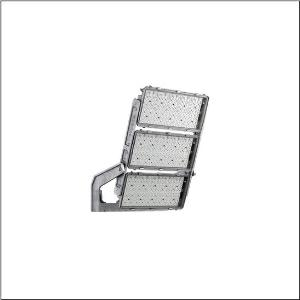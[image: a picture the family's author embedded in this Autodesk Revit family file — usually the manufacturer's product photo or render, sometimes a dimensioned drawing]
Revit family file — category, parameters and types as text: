
# Revit family: floodlight_fl_11_maxi_pro_remote___pl64blc_5xa779425w01aa_643d
name_source: partatom
category: Lighting Fixtures
units: mm (PartAtom-declared; Revit-internal decimal feet)

## family parameters
Cut with Voids When Loaded = No
Host = Face
Light Source = No
Part Type = Normal
Room Calculation Point = No
Round Connector Dimension = Use Diameter
Shared = No

## types (1)
- --- (1 x LED, 135060 lm, 1516.7 W, 3000K)
    Apparent Load = 1517 VA
    CIE Flux Codes = 28 83 99 100 100
    Color Rendering = 70
    Color Temperature = 3000K
    Default Elevation = 1800 mm
    Description = Floodlight FL 11  maxi  pro Remote floodlight; light control with lens of PMMA; cover panel of toughened safety glass, transparent; light distribution: PL64BLC, asymmetric direct distribution, LEDcolour temperature: 3000K, rated luminous flux: 135.060lm, colour rendering: CRI > 70, light colour: 730; luminous efficacy: 89lm/W; brightness control: DALI 2 (1 DALI address); with terminal, 8-pole, max. 2.5mm², mains connection: 220..240V/380..400V AC, 50/60Hz, surge voltage resistance: line to ground: 10kV, ECG replaceable separately, no afterglow with DALI off / DMX off command, LED unit replaceable without ESD environment, dustproof LED module, dimming range 10..100%; 1517W floodlight with 2x LED unit of diecast aluminium, coated grey; length: 713mm / width: 651mm / height: 338mm; mounting bracket, of diecast aluminium, uncoated, natural, equipment: Power, protection rating (complete): IP66; insulation class (complete): insulation class I (protective earthing); certification: CE, ENEC, VDE; ball protection: ball impact resistance with accessories, impact resistance: IK07; only for outdoor installations, rated ambient temperature 10°C, permissible operating ambient temperature: -40..+30°C, permissible storage temperature: -40..+85°C; packaging unit: 1 piece

Light Distribution: PL64BLC
    Height = 320 mm
    Lamp = 1 x LED
    Lamp Light Flux = 135060 lm
    Lamp Power = 1516.7 W
    Lamp count = 1
    Length = 1002 mm
    Luminous efficacy = 89 lm/W
    Manufacturer = Siteco
    ModVariant = No
    Model = 5XA779425W01AA
    Mounting Place = Ceiling
    Mounting Type = Surface mounted
    Number of Poles = 1
    OnlyDefault = Yes
    Power Factor = 1
    Product Name = Floodlight FL 11 maxi pro Remote | PL64BLC
    Product group = floodlight | ceiling mounted
    ProductGroupID = 302
    Protection Class = Protection class I
    Protection Degree = IP 66
    RLX_Detail_Level = 1
    RLX_Emergency_Light_Flux = 0 lm
    RLX_Emergency_Type = 0
    RLX_Emergency_Type_DB = No
    RlxData = <blob elided: 52317 chars, md5=75fceba1>
    Socket = socket
    Standby Power = 0 W
    System Light Flux = 135060 lm
    System Power = 1517 W
    Type Comments = factory setting: luminous flux: 100 % | dim-lin: 254 | 1070 mA
    Type Image = l_1006784.jpg
    URL = http://relux.com
    VarID = @adj_050015
    Voltage = 0 V
    Weight = 0.00 kg
    Width = 655 mm

## geometry (parser evidence)
native form markers: Blend x4, Sweep x14
no freeform markers — native parametric forms only
